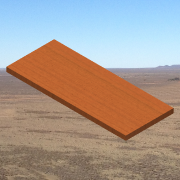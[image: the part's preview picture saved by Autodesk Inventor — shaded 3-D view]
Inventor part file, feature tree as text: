
AUTODESK INVENTOR PART (.ipt)
format: ipt  version: 2014 SP1 (Build 180222100, 222)  size: 126,464 bytes
history: native  units: in
note: dims shown in document units (in); Inventor stores cm internally (conversion verified against a paired STEP export)
features: extrude x1, sketch x1
ambient origin geometry x8: Origin, YZ Plane, XZ Plane, XY Plane, X Axis, Y Axis, Z Axis, Center Point
bodies: Solid1 (feature_tree)
feature tree (2):
  extrude  "Extrusion1"  Depth=8.0in
  sketch  "Sketch1"  dims[d0=20.0in d1=8.0in d2=0.75in d3=0.0in]
